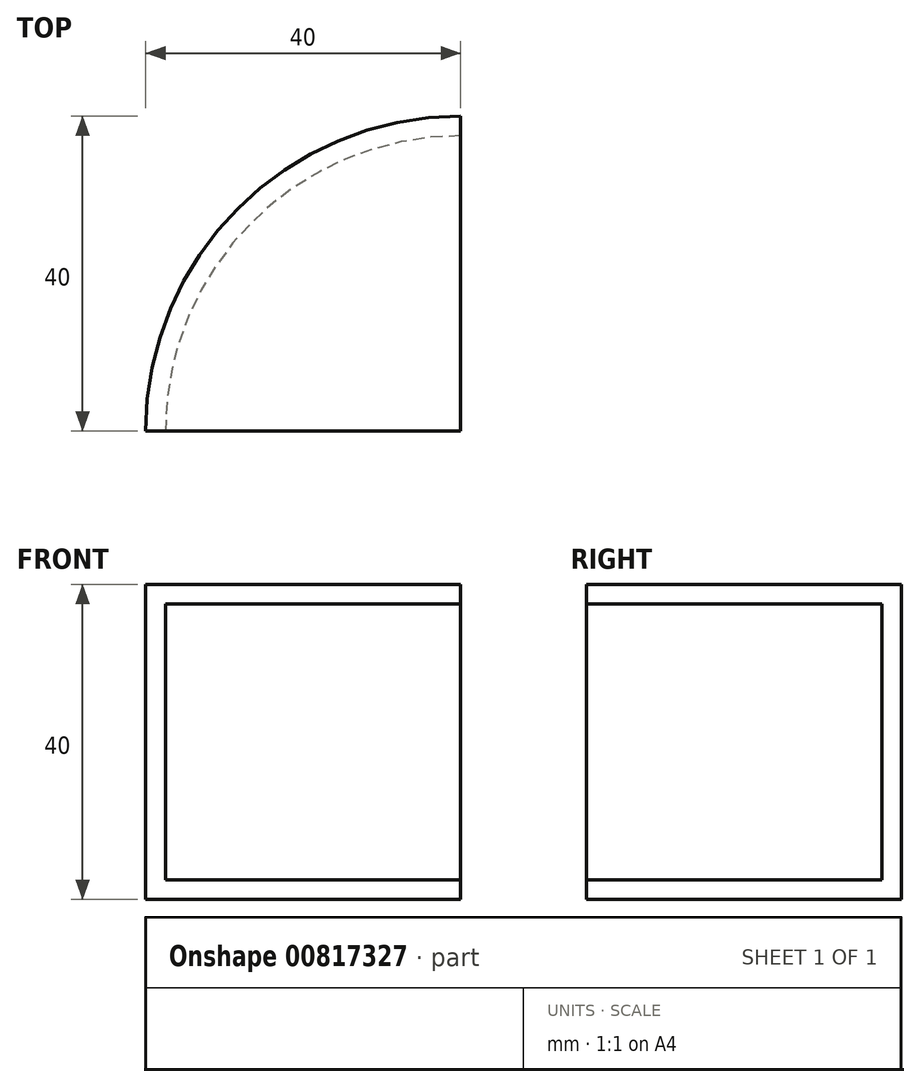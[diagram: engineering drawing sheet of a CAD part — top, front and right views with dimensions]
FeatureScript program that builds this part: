
annotation { "Feature Type Name" : "Feature", "Feature Type Description" : "" }
export const myFeature = defineFeature(function(context is Context, id is Id, definition is map)
    precondition{}
    {
        {
            var Q0;
            Q0=qCreatedBy(makeId("Top.planeOp"),FACE);
            var sketch = newSketch(context, id + "F0", { "sketchPlane" : qUnion([Q0])});
            skLineSegment(sketch, "E0", {"start": v(0, 0) * mm, "end": v(0, 40) * mm});
            skLineSegment(sketch, "E1", {"start": v(0, 0) * mm, "end": v(-40, 0) * mm});
            skArc(sketch, "E2", {"start": v(0, 40) * mm, "mid": v(-28.28, 28.28) * mm, "end": v(-40, 0) * mm});
            skSolve(sketch);
        }
        {
            var Q0;
            Q0=makeQuery(id+"F0.imprint","IMPRINT",FACE,{"disambiguationData":[TD([[makeQuery(id+"F0.imprint","IMPRINT",EDGE,{"derivedFrom":sQuery(id+"F0.wireOp",EDGE,"E0")}),1.0]])]});
            extrude(context, id + "F1", {"entities" : qUnion([Q0]), "depth" : 40 * mm, "offsetDistance" : 25 * mm});
        }
        {
            var Q0;
            Q0=makeQuery(id+"F1.opExtrude","SWEPT_FACE",FACE,{"disambiguationData":[OSD([sQuery(id+"F0.wireOp",EDGE,"E1")])]});
            var Q1;
            Q1=makeQuery(id+"F1.opExtrude","SWEPT_FACE",FACE,{"disambiguationData":[OSD([sQuery(id+"F0.wireOp",EDGE,"E0")])]});
            shell(context, id + "F2", {"entities" : qUnion([Q0, Q1]), "thickness" : 2.5 * mm});
        }
    });
